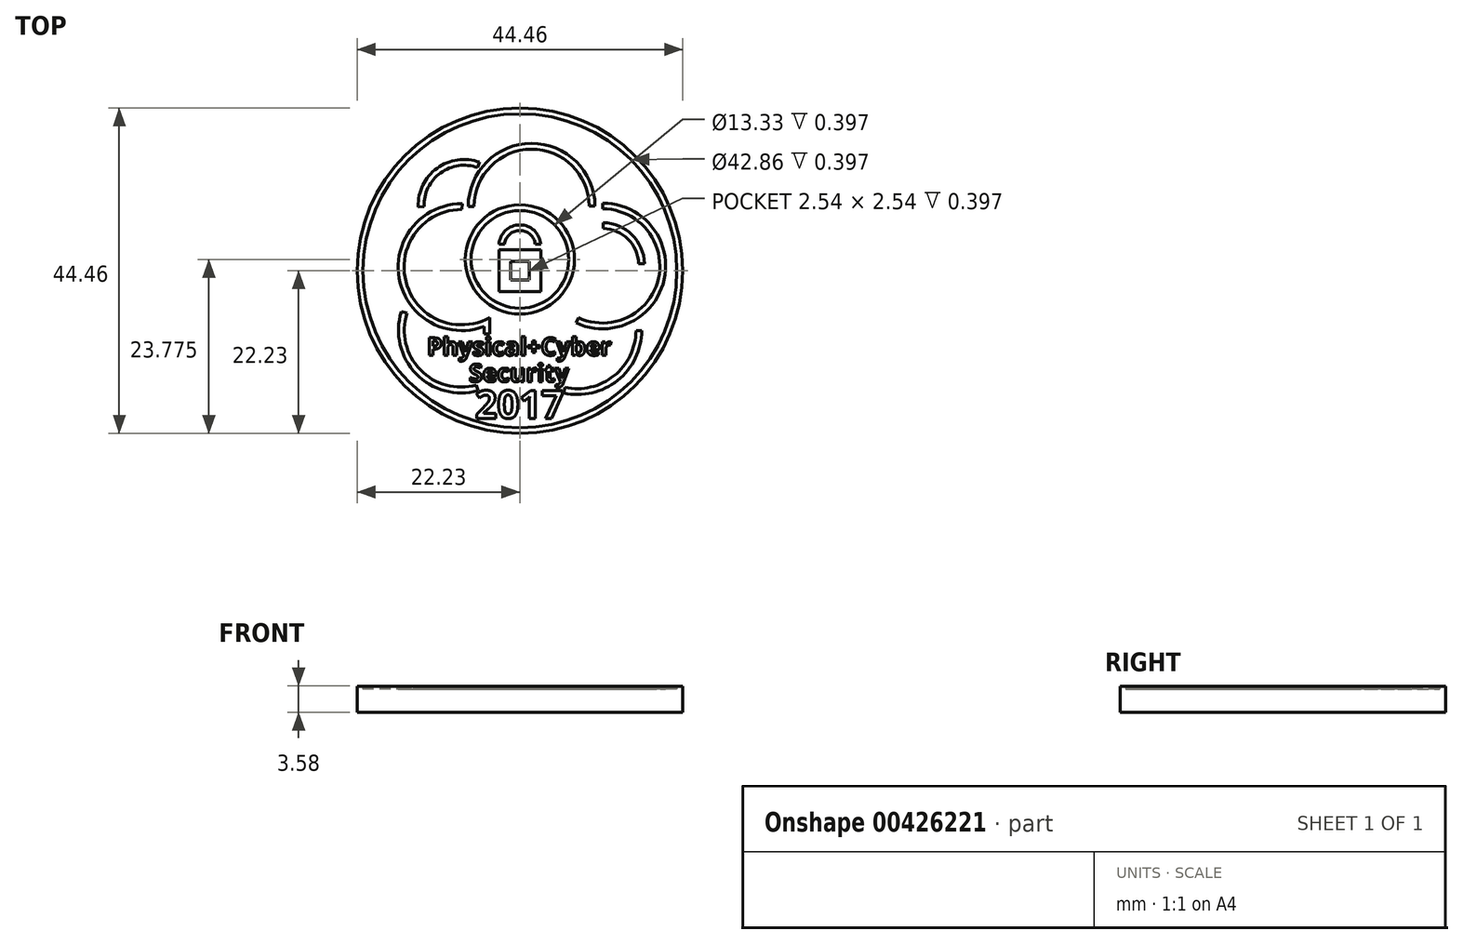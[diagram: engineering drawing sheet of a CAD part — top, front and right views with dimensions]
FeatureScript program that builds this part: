
annotation { "Feature Type Name" : "Feature", "Feature Type Description" : "" }
export const myFeature = defineFeature(function(context is Context, id is Id, definition is map)
    precondition{}
    {
        {
            var Q0;
            Q0=qCreatedBy(makeId("Top.planeOp"),FACE);
            var sketch = newSketch(context, id + "F0", { "sketchPlane" : qUnion([Q0])});
            skCircle(sketch, "E0", {"center": v(0, 0) * mm, "radius": 22.23 * mm});
            skCircle(sketch, "E1", {"center": v(-59.36, 32.28) * mm, "radius": 29.7 * mm});
            skCircle(sketch, "E2", {"center": v(-45.28, -24.63) * mm, "radius": 36.72 * mm});
            skSolve(sketch);
        }
        {
            var Q0;
            Q0=makeQuery(id+"F0.imprint","IMPRINT",FACE,{"disambiguationData":[TD([[makeQuery(id+"F0.imprint","IMPRINT",EDGE,{"derivedFrom":sQuery(id+"F0.wireOp",EDGE,"E0")}),1.0]])]});
            var Q1;
            Q1=sQuery(id+"F0.wireOp",EDGE,"E0");
            extrude(context, id + "F1", {"entities" : qUnion([Q0]), "surfaceEntities" : qUnion([Q1]), "oppositeDirection" : true, "depth" : 3.17 * mm});
        }
        {
            var Q0;
            Q0=qCreatedBy(makeId("Top.planeOp"),FACE);
            var sketch = newSketch(context, id + "F2", { "sketchPlane" : qUnion([Q0])});
            skCircle(sketch, "E3", {"center": v(0, 0) * mm, "radius": 22.23 * mm});
            skCircle(sketch, "E4", {"center": v(0, 0) * mm, "radius": 21.43 * mm});
            skSolve(sketch);
        }
        {
            var Q0;
            Q0 = qSketchRegion(id + "F2", true);
            extrude(context, id + "F3", {"entities" : qUnion([Q0]), "operationType" : NewBodyOperationType.ADD, "depth" : 0.4 * mm});
        }
        {
            var Q0;
            Q0=qCreatedBy(makeId("Top.planeOp"),FACE);
            var sketch = newSketch(context, id + "F4", { "sketchPlane" : qUnion([Q0])});
            skLineSegment(sketch, "E5.bottom", {"start": v(-2.86, 2.86) * mm, "end": v(2.86, 2.86) * mm});
            skLineSegment(sketch, "E5.top", {"start": v(-2.86, -2.86) * mm, "end": v(2.86, -2.86) * mm});
            skLineSegment(sketch, "E5.left", {"start": v(-2.86, 2.86) * mm, "end": v(-2.86, -2.86) * mm});
            skLineSegment(sketch, "E5.right", {"start": v(2.86, 2.86) * mm, "end": v(2.86, -2.86) * mm});
            skLineSegment(sketch, "E6.bottom", {"start": v(-1.27, 1.27) * mm, "end": v(1.27, 1.27) * mm});
            skLineSegment(sketch, "E6.top", {"start": v(-1.27, -1.27) * mm, "end": v(1.27, -1.27) * mm});
            skLineSegment(sketch, "E6.left", {"start": v(-1.27, 1.27) * mm, "end": v(-1.27, -1.27) * mm});
            skLineSegment(sketch, "E6.right", {"start": v(1.27, 1.27) * mm, "end": v(1.27, -1.27) * mm});
            skArc(sketch, "E7", {"start": v(2.86, 3.62) * mm, "mid": v(0, 6.26) * mm, "end": v(-2.86, 3.62) * mm});
            skArc(sketch, "E8", {"start": v(2.1, 3.62) * mm, "mid": v(0, 5.5) * mm, "end": v(-2.1, 3.62) * mm});
            skLineSegment(sketch, "E9", {"start": v(-2.86, 3.62) * mm, "end": v(-2.1, 3.62) * mm});
            skLineSegment(sketch, "E10", {"start": v(2.1, 3.62) * mm, "end": v(2.86, 3.62) * mm});
            skSolve(sketch);
        }
        {
            var Q0;
            Q0 = qSketchRegion(id + "F4", true);
            extrude(context, id + "F5", {"entities" : qUnion([Q0]), "operationType" : NewBodyOperationType.ADD, "depth" : 0.4 * mm});
        }
        {
            var Q0;
            Q0=qCreatedBy(makeId("Top.planeOp"),FACE);
            var sketch = newSketch(context, id + "F6", { "sketchPlane" : qUnion([Q0])});
            skText(sketch, "E11", { "text": "Physical+Cyber\n", "fontName": "OpenSans-Bold.ttf"});
            skText(sketch, "E12", { "text": "Security", "fontName": "OpenSans-Bold.ttf"});
            skText(sketch, "E13", { "text": "2017", "fontName": "OpenSans-Bold.ttf"});
            const initialGuessF6  = {"E11": [-0.0127, -0.01156, 1, 0, 0.00241], "E12": [-0.00694, -0.01516, 1, 0, 0.00241], "E13": [-0.00613, -0.02016, 1, 0, 0.00381]};
            skSetInitialGuess(sketch, initialGuessF6);
            skSolve(sketch);
        }
        {
            var Q0;
            Q0 = qSketchRegion(id + "F6", true);
            extrude(context, id + "F7", {"entities" : qUnion([Q0]), "operationType" : NewBodyOperationType.ADD, "depth" : 0.4 * mm});
        }
        {
            var Q0;
            Q0=qCreatedBy(makeId("Top.planeOp"),FACE);
            var sketch = newSketch(context, id + "F8", { "sketchPlane" : qUnion([Q0])});
            skText(sketch, "E14", { "text": "Technology Innovation", "fontName": "OpenSans-Bold.ttf"});
            skText(sketch, "E15", { "text": "Accelerator", "fontName": "OpenSans-Bold.ttf"});
            const initialGuessF8  = {"E14": [-0.01254, 0.01238, 1, 0, 0.00159], "E15": [-0.00641, 0.01, 1, 0, 0.00159]};
            skSetInitialGuess(sketch, initialGuessF8);
            skSolve(sketch);
        }
        {
            var Q0;
            Q0=qCreatedBy(makeId("Top.planeOp"),FACE);
            var sketch = newSketch(context, id + "F9", { "sketchPlane" : qUnion([Q0])});
            skCircle(sketch, "E16", {"center": v(0, 1.54) * mm, "radius": 6.67 * mm});
            skPoint(sketch, "E16.first.point", {"position": v(-6.16, 4.1) * mm});
            skPoint(sketch, "E16.second.point", {"position": v(6.22, -0.87) * mm});
            skPoint(sketch, "E16.third.point", {"position": v(0, -5.12) * mm});
            skCircle(sketch, "E17.0", {"center": v(0, 1.54) * mm, "radius": 7.46 * mm});
            skArc(sketch, "E18", {"start": v(9.47, 8.83) * mm, "mid": v(1.57, 16.6) * mm, "end": v(-6.26, 8.77) * mm});
            skArc(sketch, "E19", {"start": v(-7.9, 8.36) * mm, "mid": v(-15.58, -1.48) * mm, "end": v(-4.1, -6.38) * mm});
            skArc(sketch, "E20", {"start": v(-15.43, -5.8) * mm, "mid": v(-13.61, -13.54) * mm, "end": v(-5.95, -15.62) * mm});
            skArc(sketch, "E21", {"start": v(6.15, -15.94) * mm, "mid": v(12.84, -14.36) * mm, "end": v(15.85, -8.17) * mm});
            skArc(sketch, "E22", {"start": v(16.2, 0.97) * mm, "mid": v(14.76, 4.34) * mm, "end": v(11.38, 5.76) * mm});
            skArc(sketch, "E23", {"start": v(8, -6.4) * mm, "mid": v(18.92, -1.04) * mm, "end": v(11.3, 8.45) * mm});
            skArc(sketch, "E24", {"start": v(-5.77, 14.09) * mm, "mid": v(-10.84, 13.36) * mm, "end": v(-13.1, 8.76) * mm});
            skArc(sketch, "E25.0", {"start": v(-5.5, 14.83) * mm, "mid": v(-11.3, 14) * mm, "end": v(-13.89, 8.73) * mm});
            skArc(sketch, "E26.0", {"start": v(10.26, 8.84) * mm, "mid": v(1.57, 17.4) * mm, "end": v(-7.06, 8.77) * mm});
            skArc(sketch, "E27.0", {"start": v(7.66, -7.12) * mm, "mid": v(19.7, -1.22) * mm, "end": v(11.3, 9.24) * mm});
            skArc(sketch, "E28.0", {"start": v(5.98, -16.72) * mm, "mid": v(13.34, -14.98) * mm, "end": v(16.64, -8.18) * mm});
            skArc(sketch, "E29.0", {"start": v(-16.2, -5.57) * mm, "mid": v(-14.18, -14.09) * mm, "end": v(-5.73, -16.38) * mm});
            skArc(sketch, "E30.0", {"start": v(-7.9, 9.16) * mm, "mid": v(-16.49, -1.04) * mm, "end": v(-4.9, -7.63) * mm});
            skArc(sketch, "E31.0", {"start": v(17, 0.99) * mm, "mid": v(15.32, 4.9) * mm, "end": v(11.39, 6.55) * mm});
            skLineSegment(sketch, "E32", {"start": v(-5.5, 14.83) * mm, "end": v(-5.77, 14.09) * mm});
            skLineSegment(sketch, "E33", {"start": v(-13.89, 8.73) * mm, "end": v(-13.1, 8.76) * mm});
            skLineSegment(sketch, "E34", {"start": v(-7.06, 8.77) * mm, "end": v(-6.26, 8.77) * mm});
            skLineSegment(sketch, "E35", {"start": v(9.47, 8.83) * mm, "end": v(10.26, 8.84) * mm});
            skLineSegment(sketch, "E36", {"start": v(11.3, 9.24) * mm, "end": v(11.3, 8.45) * mm});
            skLineSegment(sketch, "E37", {"start": v(8, -6.4) * mm, "end": v(7.66, -7.12) * mm});
            skLineSegment(sketch, "E38", {"start": v(16.2, 0.97) * mm, "end": v(17, 0.99) * mm});
            skLineSegment(sketch, "E39", {"start": v(11.39, 6.55) * mm, "end": v(11.38, 5.76) * mm});
            skLineSegment(sketch, "E40", {"start": v(-7.9, 9.16) * mm, "end": v(-7.9, 8.36) * mm});
            skLineSegment(sketch, "E41", {"start": v(-5.95, -15.62) * mm, "end": v(-5.73, -16.38) * mm});
            skLineSegment(sketch, "E42", {"start": v(-16.2, -5.57) * mm, "end": v(-15.43, -5.8) * mm});
            skLineSegment(sketch, "E43", {"start": v(6.15, -15.94) * mm, "end": v(5.98, -16.72) * mm});
            skLineSegment(sketch, "E44", {"start": v(15.85, -8.17) * mm, "end": v(16.64, -8.18) * mm});
            skLineSegment(sketch, "E45", {"start": v(-4.9, -7.63) * mm, "end": v(-4.9, -8.63) * mm});
            skLineSegment(sketch, "E46", {"start": v(-4.1, -8.63) * mm, "end": v(-4.1, -6.38) * mm});
            skLineSegment(sketch, "E47", {"start": v(-4.9, -8.63) * mm, "end": v(-4.1, -8.63) * mm});
            skPoint(sketch, "E48.orphan", {"position": v(-4.1, -8.68) * mm});
            skPoint(sketch, "E49.orphan", {"position": v(-4.9, -7.12) * mm});
            skSolve(sketch);
        }
        {
            var Q0;
            Q0 = qSketchRegion(id + "F9", true);
            extrude(context, id + "F10", {"entities" : qUnion([Q0]), "operationType" : NewBodyOperationType.ADD, "depth" : 0.4 * mm});
        }
    });
